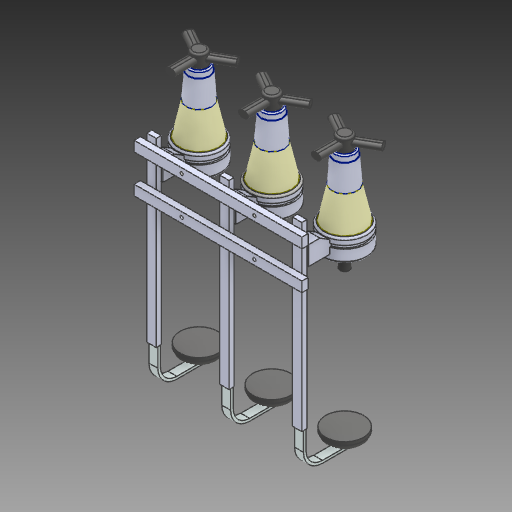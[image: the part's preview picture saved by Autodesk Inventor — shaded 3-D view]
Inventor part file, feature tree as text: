
AUTODESK INVENTOR PART (.ipt)
format: ipt  version: 2017 (Build 210142000, 142)  size: 602,112 bytes
history: mixed  units: mm
features: other x6, mirror x3, fillet x2, revolve x1, imported_body x1
ambient origin geometry x8: Origin, YZ Plane, XZ Plane, XY Plane, X Axis, Y Axis, Z Axis, Center Point
bodies: Solid1 (imported_parasolid), Solid2 (imported_parasolid), Solid3 (imported_parasolid), Solid4 (imported_parasolid), Solid5 (imported_parasolid), Solid6 (imported_parasolid), Solid7 (imported_parasolid), Solid8 (imported_parasolid), Solid9 (imported_parasolid), Solid10 (imported_parasolid), Solid11 (imported_parasolid), Solid12 (imported_parasolid)
feature tree (13):
  revolve  "Revolve1"  [1 undecoded]
  fillet  "Fillet4"  [1 undecoded]
  fillet  "Fillet6"  [1 undecoded]
  other  "LPattern12[1]"
  other  "LPattern12[2]"
  other  "LPattern12[3]"
  mirror  "Mirror2[1]"
  mirror  "Mirror2[2]"
  mirror  "Mirror2[3]"
  other  "LPattern13[1]"
  other  "LPattern13[2]"
  other  "LPattern13[3]"
  imported_body  NMx_Import_Brep_tag  [imported B-rep: ~45 faces, bbox_mm=None]
note: 3 required parameter values undecoded (feature->parameter linkage not recoverable at this tier; creation-order binding heuristic only, values carry confidence <= 0.55)
